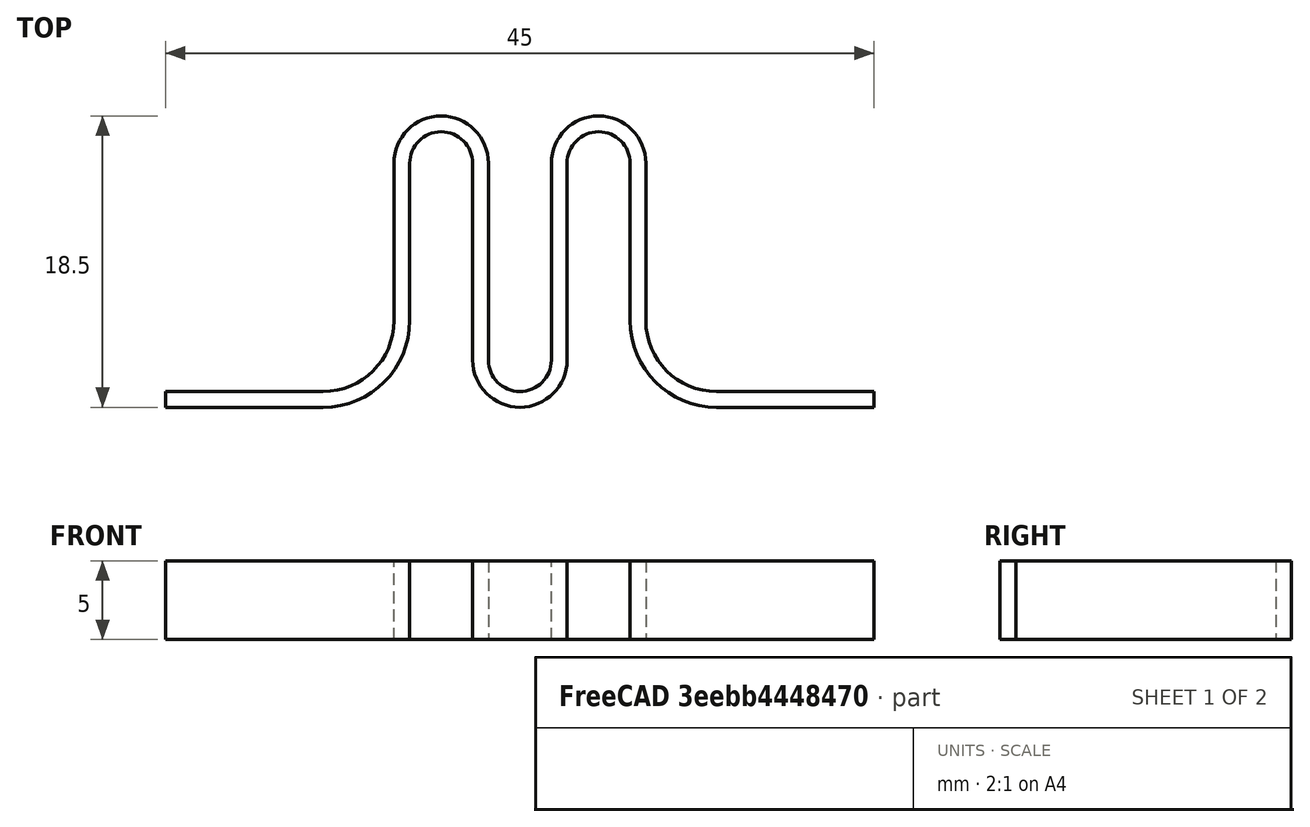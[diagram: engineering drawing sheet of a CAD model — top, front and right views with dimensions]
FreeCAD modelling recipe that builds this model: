
FCSTD DOCUMENT  (FreeCAD 2021.1015R24301 +3962 (Git))
Label: plastic_spring_double_loop
License: All rights reserved
objects: Sketcher::SketchObject×2, Mesh::Feature×2, Spreadsheet::Sheet×1, PartDesign::AdditivePipe×1, PartDesign::Body×1
note: 6 computed .brp shape members not serialized (recipe doc carries the construction recipe); baked Part::Feature solids carry a one-line shape summary decoded from their .brp

FEATURE [Spreadsheet::Sheet] Spreadsheet
  PythonMode = false
  cells = A1='height; B1(h)=5; A2='thickness; B2(thk)=1; A3='dia; B3(dia)=5; A4=start finish rad; B4(r_start)=5; A5=center length; B5(l_center)=15; A6=center spacing; B6(cs)=7; C6=should be dia/2 really; A7=end length; B7(l_end)=10
FEATURE [Sketcher::SketchObject] Sketch  label="profile"
  FullyConstrained = true
  MapMode = 5
  Placement = pos=(0,0,0) rot=(0.57735,0.57735,0.57735;2.0944rad)
  Support = -> [YZ_Plane]
  expr: Constraints[10] = Spreadsheet.thk / 2
  expr: Constraints[11] = Spreadsheet.thk
  expr: Constraints[9] = Spreadsheet.h
  sketch-geometry (4):
    g0: LineSegment StartX=-0.5 StartY=0 StartZ=0 EndX=0.5 EndY=0 EndZ=0
    g1: LineSegment StartX=0.5 StartY=0 StartZ=0 EndX=0.5 EndY=5 EndZ=0
    g2: LineSegment StartX=0.5 StartY=5 StartZ=0 EndX=-0.5 EndY=5 EndZ=0
    g3: LineSegment StartX=-0.5 StartY=5 StartZ=0 EndX=-0.5 EndY=0 EndZ=0
  constraints (12):
    c: Coincident(g0,g1)
    c: Coincident(g1,g2)
    c: Coincident(g2,g3)
    c: Coincident(g3,g0)
    c: Horizontal(g0)
    c: Horizontal(g2)
    c: Vertical(g1)
    c: Vertical(g3)
    c: PointOnObject(g0,g-1)
    c: DistanceY(g3,g3) = 5
    c: DistanceX(g0,g-1) = 0.5
    c: DistanceX(g0,g0) = 1
FEATURE [Sketcher::SketchObject] Sketch001  label="path"
  FullyConstrained = true
  MapMode = 5
  Support = -> [XY_Plane]
  expr: Constraints[12] = Spreadsheet.l_end
  expr: Constraints[13] = Spreadsheet.dia
  expr: Constraints[14] = Spreadsheet.l_end
  expr: Constraints[15] = Spreadsheet.r_start
  expr: Constraints[16] = Spreadsheet.l_center
  expr: Constraints[17] = Spreadsheet.dia
  expr: Constraints[32] = Spreadsheet.dia
  expr: Constraints[33] = Spreadsheet.dia
  expr: Constraints[36] = Spreadsheet.r_start
  sketch-geometry (12):
    g0: LineSegment StartX=0 StartY=0 StartZ=0 EndX=10 EndY=0 EndZ=0
    g1: LineSegment StartX=15 StartY=5 StartZ=0 EndX=15 EndY=15 EndZ=0
    g2: ArcOfCircle CenterX=9.99999 CenterY=5 CenterZ=0 NormalX=0 NormalY=0 NormalZ=1 AngleXU=0 Radius=5 StartAngle=4.71239 EndAngle=6.28319
    g3: ArcOfCircle CenterX=17.5 CenterY=15 CenterZ=0 NormalX=0 NormalY=0 NormalZ=1 AngleXU=0 Radius=2.5 StartAngle=4.49312e-06 EndAngle=3.14159
    g4: LineSegment StartX=20 StartY=15 StartZ=0 EndX=20 EndY=2.5 EndZ=0
    g5: LineSegment StartX=35 StartY=0 StartZ=0 EndX=45 EndY=0 EndZ=0
    g6: ArcOfCircle CenterX=22.5 CenterY=2.5 CenterZ=0 NormalX=0 NormalY=0 NormalZ=1 AngleXU=0 Radius=2.5 StartAngle=3.14159 EndAngle=6.28319
    g7: LineSegment StartX=25 StartY=2.5 StartZ=0 EndX=25 EndY=15 EndZ=0
    g8: LineSegment StartX=30 StartY=15 StartZ=0 EndX=30 EndY=5 EndZ=0
    g9: ArcOfCircle CenterX=27.5 CenterY=15 CenterZ=0 NormalX=0 NormalY=0 NormalZ=1 AngleXU=0 Radius=2.5 StartAngle=4.49208e-06 EndAngle=3.14159
    g10: ArcOfCircle CenterX=35 CenterY=5 CenterZ=0 NormalX=0 NormalY=0 NormalZ=1 AngleXU=0 Radius=5 StartAngle=3.14159 EndAngle=4.71239
    g11: LineSegment [constr] StartX=17.5 StartY=15 StartZ=0 EndX=27.5 EndY=15 EndZ=0
  constraints (40):
    c: Coincident(g0,g-1)
    c: PointOnObject(g0,g-1)
    c: Coincident(g2,g0)
    c: Coincident(g2,g1)
    c: Coincident(g3,g1)
    c: Coincident(g4,g3)
    c: PointOnObject(g5,g-1)
    c: PointOnObject(g5,g-1)
    c: Tangent(g0,g2)
    c: Tangent(g2,g1)
    c: Tangent(g1,g3)
    c: Tangent(g3,g4)
    c: DistanceX(g5,g5) = 10
    c: Diameter(g3) = 5
    c: DistanceX(g0,g0) = 10
    c: Radius(g2) = 5
    c: DistanceY(g0,g3) = 15
    c: DistanceX(g1,g4) = 5
    c: Vertical(g1)
    c: Coincident(g6,g4)
    c: Tangent(g6,g-1)
    c: Coincident(g7,g6)
    c: Vertical(g7)
    c: Vertical(g8)
    c: Coincident(g9,g7)
    c: Coincident(g9,g8)
    c: Coincident(g10,g8)
    c: Coincident(g10,g5)
    c: Tangent(g8,g9)
    c: Tangent(g7,g9)
    c: Tangent(g6,g7)
    c: Tangent(g6,g4)
    c: Diameter(g9) = 5
    c: Diameter(g6) = 5
    c: Tangent(g10,g8)
    c: Tangent(g10,g5)
    c: Radius(g10) = 5
    c: Coincident(g11,g3)
    c: Coincident(g11,g9)
    c: Horizontal(g11)
FEATURE [PartDesign::AdditivePipe] AdditivePipe
  AuxilleryCurvelinear = true
  AuxillerySpineTangent = false
  Binormal = (0,0,0)
  ClaimChildren = false
  Fit = 0
  FitJoin = 0
  InnerFit = 0
  InnerFitJoin = 0
  Mode = 0
  NewSolid = false
  Placement = pos=(0,0,0) rot=(0.57735,0.57735,0.57735;2.0944rad)
  Profile = -> Sketch
  Spine = -> Sketch001
  SpineTangent = false
  Suppress = false
  Transformation = 0
  Transition = 1
  _ProfileBasedVersion = 1
FEATURE [PartDesign::Body] Body
  AutoGroupSolids = false
  ExportMode = 0
  Group = -> [Sketch,Sketch001,AdditivePipe]
  Origin = -> Origin
  Tip = -> AdditivePipe
  _ExportChildren = -> [AdditivePipe]
  _GroupVersion = 1
FEATURE [Mesh::Feature] Mesh  label="double_loop_30x5"
FEATURE [Mesh::Feature] Mesh001  label="double_loop_15x5"
